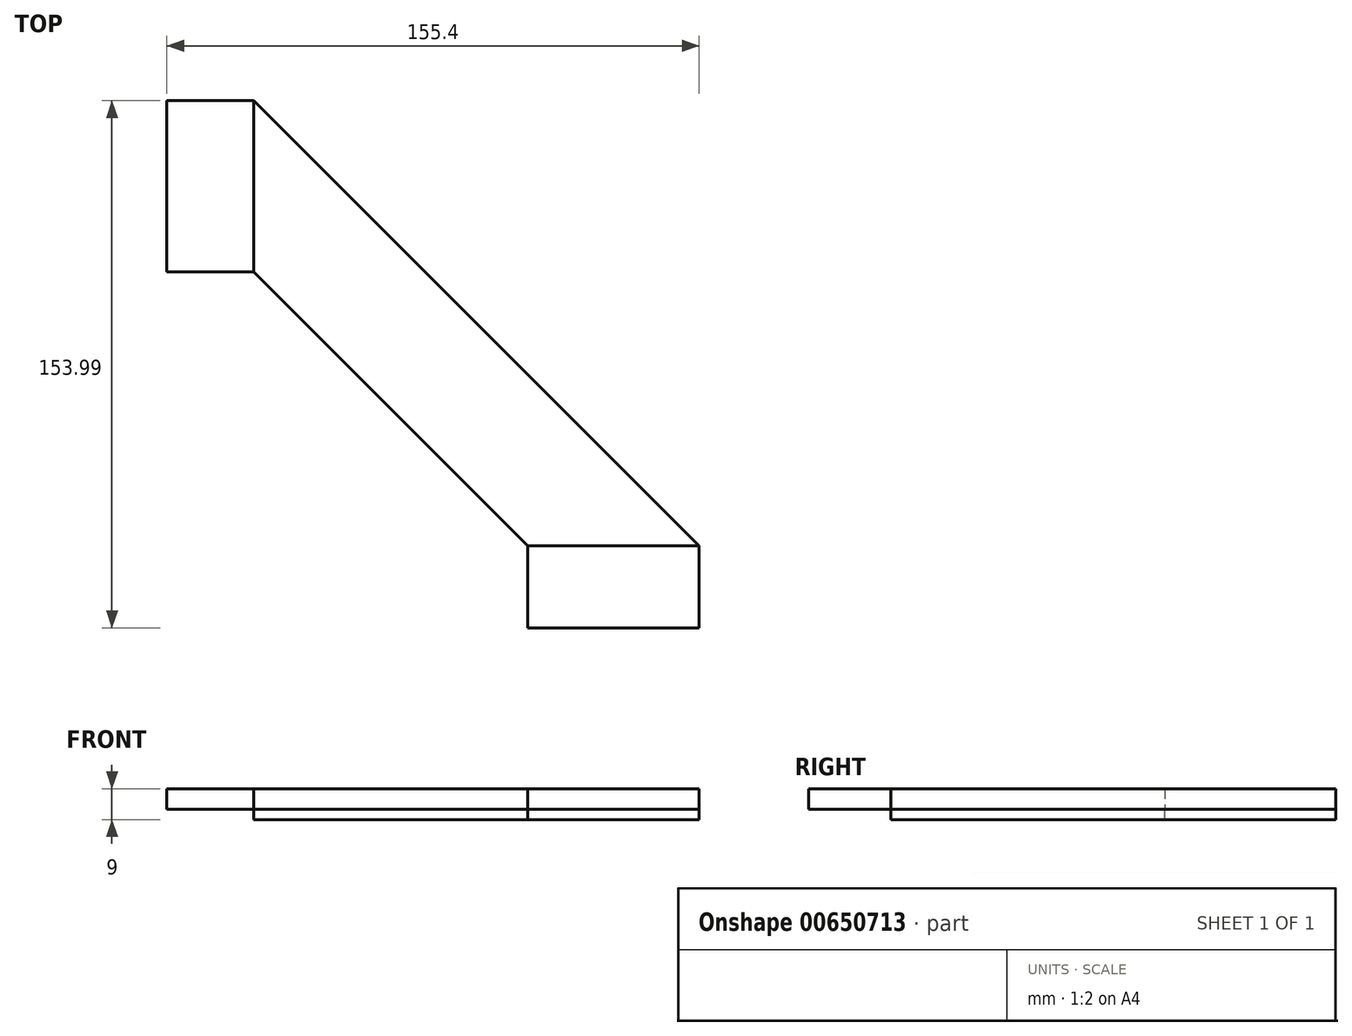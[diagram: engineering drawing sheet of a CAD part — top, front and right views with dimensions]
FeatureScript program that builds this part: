
annotation { "Feature Type Name" : "Feature", "Feature Type Description" : "" }
export const myFeature = defineFeature(function(context is Context, id is Id, definition is map)
    precondition{}
    {
        {
            var Q0;
            Q0=qCreatedBy(makeId("Top.planeOp"),FACE);
            var sketch = newSketch(context, id + "F0", { "sketchPlane" : qUnion([Q0])});
            skLineSegment(sketch, "E0.bottom", {"start": v(101.17, -76.02) * mm, "end": v(-101.17, -76.02) * mm, "construction": true});
            skLineSegment(sketch, "E0.top", {"start": v(101.17, 76.02) * mm, "end": v(-101.17, 76.02) * mm});
            skLineSegment(sketch, "E0.left", {"start": v(101.17, -76.02) * mm, "end": v(101.17, 76.02) * mm});
            skLineSegment(sketch, "E0.right", {"start": v(-101.17, -76.02) * mm, "end": v(-101.17, 76.02) * mm, "construction": true});
            skPoint(sketch, "E0.middle", {"position": v(0, 0) * mm});
            skPoint(sketch, "E1", {"position": v(-21.17, -76.02) * mm});
            skPoint(sketch, "E2", {"position": v(-101.17, 3.98) * mm});
            skPoint(sketch, "E3", {"position": v(28.83, -76.02) * mm});
            skPoint(sketch, "E4", {"position": v(-101.17, 53.98) * mm});
            skLineSegment(sketch, "E5", {"start": v(-101.17, 3.98) * mm, "end": v(-101.17, 53.98) * mm});
            skLineSegment(sketch, "E6", {"start": v(-21.17, -76.02) * mm, "end": v(28.83, -76.02) * mm});
            skLineSegment(sketch, "E7", {"start": v(-101.17, 53.98) * mm, "end": v(28.83, -76.02) * mm});
            skLineSegment(sketch, "E8", {"start": v(-21.17, -76.02) * mm, "end": v(-101.17, 3.98) * mm});
            skLineSegment(sketch, "E9", {"start": v(-101.17, 53.98) * mm, "end": v(-126.57, 53.98) * mm});
            skLineSegment(sketch, "E10", {"start": v(-126.57, 53.98) * mm, "end": v(-126.57, 3.98) * mm});
            skLineSegment(sketch, "E11", {"start": v(-126.57, 3.98) * mm, "end": v(-101.17, 3.98) * mm});
            skLineSegment(sketch, "E12", {"start": v(-21.17, -76.02) * mm, "end": v(-21.17, -100.01) * mm});
            skLineSegment(sketch, "E13", {"start": v(-21.17, -100.01) * mm, "end": v(28.83, -100.01) * mm});
            skLineSegment(sketch, "E14", {"start": v(28.83, -100.01) * mm, "end": v(28.83, -76.02) * mm});
            skSolve(sketch);
        }
        {
            var Q0;
            Q0=makeQuery(id+"F0.imprint","IMPRINT",FACE,{"disambiguationData":[TD([[makeQuery(id+"F0.imprint","IMPRINT",EDGE,{"derivedFrom":sQuery(id+"F0.wireOp",EDGE,"E5")}),-1.0]])]});
            extrude(context, id + "F1", {"entities" : qUnion([Q0]), "oppositeDirection" : true, "depth" : 3 * mm, "offsetDistance" : 25 * mm});
        }
        {
            var Q0;
            Q0=makeQuery(id+"F0.imprint","IMPRINT",FACE,{"disambiguationData":[TD([[makeQuery(id+"F0.imprint","IMPRINT",EDGE,{"derivedFrom":sQuery(id+"F0.wireOp",EDGE,"E5")}),1.0]])]});
            var Q1;
            Q1=makeQuery(id+"F0.imprint","IMPRINT",FACE,{"disambiguationData":[TD([[makeQuery(id+"F0.imprint","IMPRINT",EDGE,{"derivedFrom":sQuery(id+"F0.wireOp",EDGE,"E6")}),-1.0]])]});
            extrude(context, id + "F2", {"entities" : qUnion([Q0, Q1]), "operationType" : NewBodyOperationType.ADD, "depth" : 6 * mm, "offsetDistance" : 25 * mm});
        }
        {
            var Q0;
            Q0=makeQuery(id+"F2.opExtrude","SWEPT_FACE",FACE,{"disambiguationData":[OSD([sQuery(id+"F0.wireOp",EDGE,"E5")])]});
            var Q1;
            Q1=makeQuery(id+"F2.opExtrude","SWEPT_FACE",FACE,{"disambiguationData":[OSD([sQuery(id+"F0.wireOp",EDGE,"E6")])]});
            loft(context, id + "F3", {"sheetProfilesArray" : [{ "sheetProfileEntities" : qUnion([Q0]) }, { "sheetProfileEntities" : qUnion([Q1]) }]});
        }
    });
